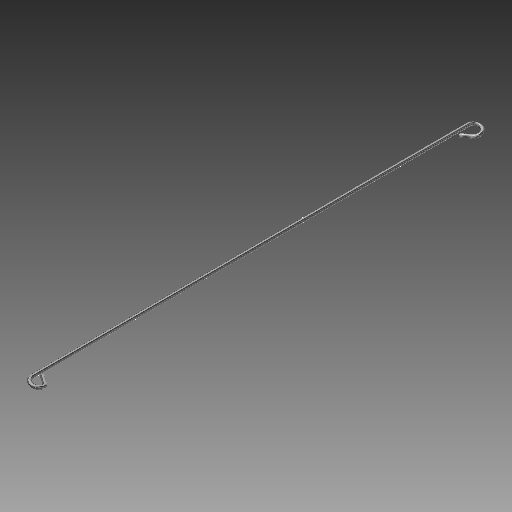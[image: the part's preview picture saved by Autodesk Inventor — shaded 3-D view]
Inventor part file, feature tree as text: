
AUTODESK INVENTOR PART (.ipt)
format: ipt  version: 2019 (Build 230136000, 136)  size: 164,864 bytes
history: native  units: mm
features: sketch x4, extrude x2, other x2, helix x1, fillet x1, mirror x1
ambient origin geometry x8: Origin, YZ Plane, XZ Plane, XY Plane, X Axis, Y Axis, Z Axis, Center Point
bodies: Solid1 (feature_tree)
feature tree (11):
  extrude  "Extrusion1"  Depth=260.0mm TaperAngle=0.0deg
  sketch  "Sketch4"  dims[d10=4.0mm d11=10.0mm d12=6.5mm d13=0.0mm d14=90.0deg d15=90.0deg d16=0.0mm d17=0.0mm d18=6.0mm d19=0.0mm d20=0.5mm d21=1.0mm]
  sketch  "Sketch5"
  other  "Work Axis1"
  helix  "Coil1"  [1 undecoded]
  extrude  "Extrusion2"  Depth=6.0mm TaperAngle=0.0deg
  fillet  "Fillet1"  Radius=0.5mm
  mirror  "Mirror1"
  sketch  "Sketch1"  dims[d0=2.032mm d3=260.0mm d4=0.0mm d9=3.266mm]
  other  "Work Point1"
  sketch  "Sketch6"
note: 1 required parameter value undecoded (feature->parameter linkage not recoverable at this tier; creation-order binding heuristic only, values carry confidence <= 0.55)
